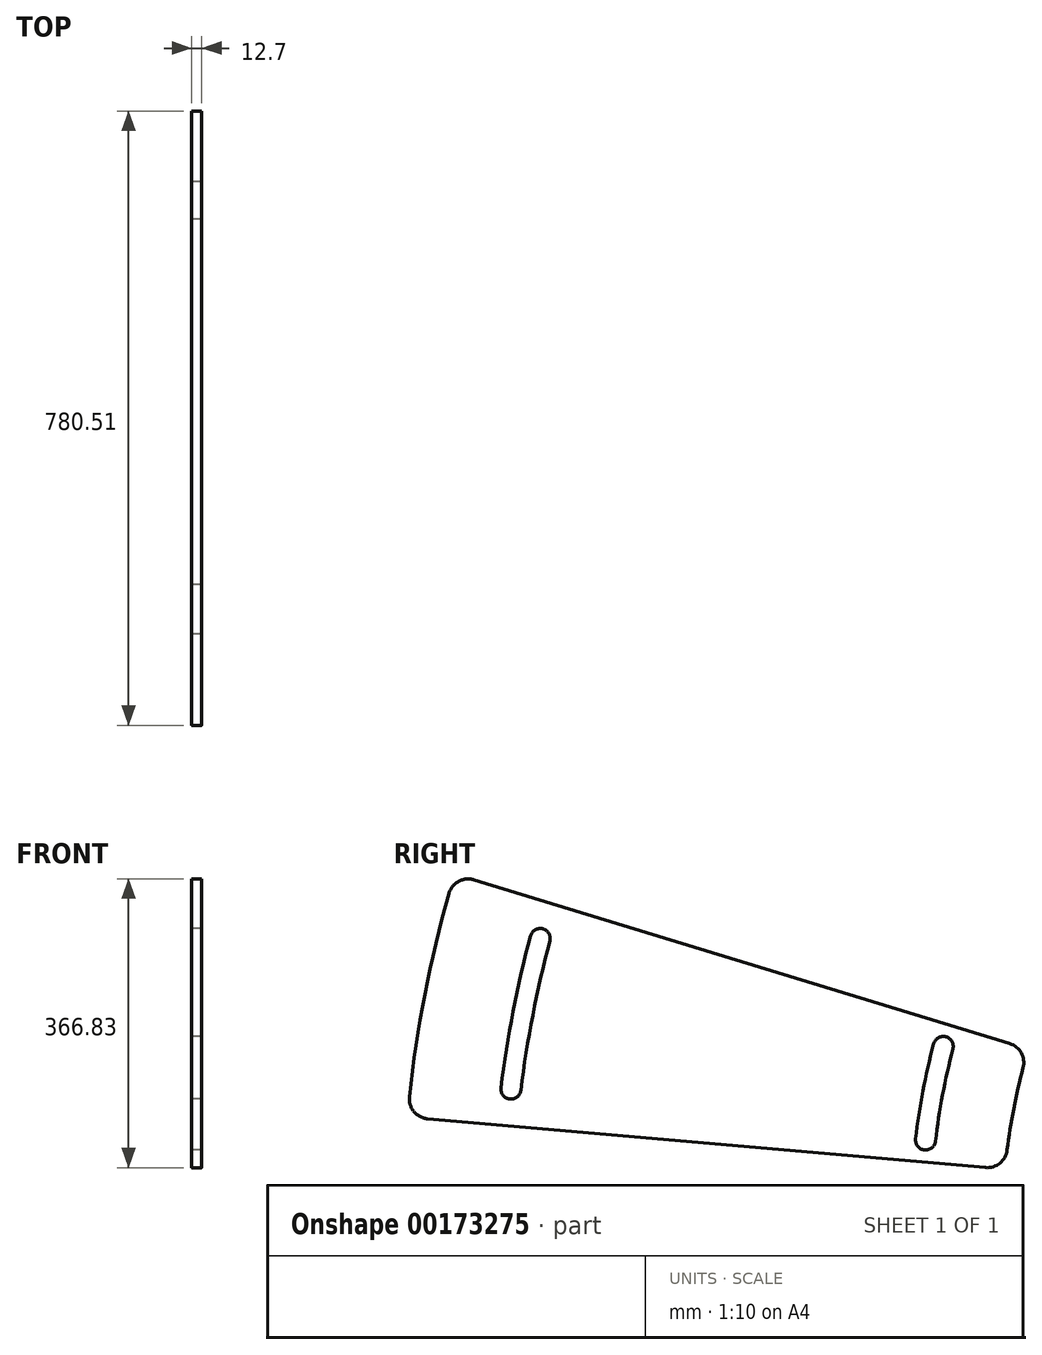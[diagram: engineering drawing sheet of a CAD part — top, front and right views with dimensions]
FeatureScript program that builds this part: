
annotation { "Feature Type Name" : "Feature", "Feature Type Description" : "" }
export const myFeature = defineFeature(function(context is Context, id is Id, definition is map)
    precondition{}
    {
        {
            var Q0;
            Q0=qCreatedBy(makeId("Right.planeOp"),FACE);
            var sketch = newSketch(context, id + "F0", { "sketchPlane" : qUnion([Q0])});
            skArc(sketch, "E0", {"start": v(-736.01, 197.3) * mm, "mid": v(-748, 145.4) * mm, "end": v(-756.33, 92.77) * mm});
            skLineSegment(sketch, "E1", {"start": v(0, 0) * mm, "end": v(-6.79, 0) * mm, "construction": true});
            skLineSegment(sketch, "E2", {"start": v(0, 0) * mm, "end": v(-1486.5, 288.95) * mm, "construction": true});
            skArc(sketch, "E3", {"start": v(-1465.3, 418.87) * mm, "mid": v(-1496, 290.8) * mm, "end": v(-1515.52, 160.55) * mm});
            skLineSegment(sketch, "E4", {"start": v(22.77, 0) * mm, "end": v(-18.63, 3.62) * mm});
            skArc(sketch, "E5", {"start": v(-837.45, 224.4) * mm, "mid": v(-850.72, 165.37) * mm, "end": v(-859.94, 105.59) * mm, "construction": true});
            skArc(sketch, "E6", {"start": v(-1349.4, 361.57) * mm, "mid": v(-1371.33, 266.56) * mm, "end": v(-1386.59, 170.25) * mm, "construction": true});
            skLineSegment(sketch, "E7.MirrorCS", {"start": v(21.1, -8.53) * mm, "end": v(-18.63, 3.62) * mm});
            skLineSegment(sketch, "E8.trimOffspring", {"start": v(-753.12, 228.18) * mm, "end": v(-1433.46, 436.18) * mm});
            skLineSegment(sketch, "E9.trimOffspring", {"start": v(-783.76, 70.56) * mm, "end": v(-1492.48, 132.57) * mm});
            skLineSegment(sketch, "E10.trimOffspring", {"start": v(-762, 0) * mm, "end": v(-1563.5, 0) * mm, "construction": true});
            skPoint(sketch, "E11.orphan", {"position": v(-1640.89, 499.6) * mm});
            skLineSegment(sketch, "E12", {"start": v(0, 0) * mm, "end": v(-1563.38, 191.96) * mm, "construction": true});
            skLineSegment(sketch, "E13", {"start": v(0, 0) * mm, "end": v(0, 0) * mm});
            skLineSegment(sketch, "E14.MirrorCS", {"start": v(0, 0) * mm, "end": v(-1521.45, 407.67) * mm, "construction": true});
            skArc(sketch, "E15.trimOffspring", {"start": v(-862.85, 77.48) * mm, "mid": v(-865.39, 38.78) * mm, "end": v(-866.23, 0) * mm, "construction": true});
            skArc(sketch, "E16.trimOffspring", {"start": v(-1391.5, 123.73) * mm, "mid": v(1371.33, -266.56) * mm, "end": v(-1336.54, 406.55) * mm, "construction": true});
            skArc(sketch, "E17.0.startCap", {"start": v(-1361.67, 364.86) * mm, "mid": v(-1346.11, 373.84) * mm, "end": v(-1337.13, 358.28) * mm});
            skArc(sketch, "E17.0.endCap", {"start": v(-1373.98, 168.7) * mm, "mid": v(-1388.13, 157.65) * mm, "end": v(-1399.2, 171.8) * mm});
            skArc(sketch, "E17.0.left", {"start": v(-1337.13, 358.28) * mm, "mid": v(-1358.87, 264.14) * mm, "end": v(-1373.98, 168.7) * mm});
            skArc(sketch, "E17.0.right", {"start": v(-1361.67, 364.86) * mm, "mid": v(-1383.8, 268.98) * mm, "end": v(-1399.2, 171.8) * mm});
            skArc(sketch, "E18.0.startCap", {"start": v(-849.74, 227.6) * mm, "mid": v(-834.24, 236.68) * mm, "end": v(-825.16, 221.19) * mm});
            skArc(sketch, "E18.0.endCap", {"start": v(-847.33, 104.08) * mm, "mid": v(-861.45, 92.98) * mm, "end": v(-872.55, 107.1) * mm});
            skArc(sketch, "E18.0.left", {"start": v(-825.16, 221.19) * mm, "mid": v(-838.24, 163.01) * mm, "end": v(-847.33, 104.08) * mm});
            skArc(sketch, "E18.0.right", {"start": v(-849.74, 227.6) * mm, "mid": v(-863.2, 167.74) * mm, "end": v(-872.55, 107.1) * mm});
            skPoint(sketch, "E19.visualSharp", {"position": v(-1457.99, 443.68) * mm});
            skArc(sketch, "E19.filletArc", {"start": v(-1433.46, 436.18) * mm, "mid": v(-1453.01, 434.2) * mm, "end": v(-1465.3, 418.87) * mm});
            skPoint(sketch, "E20.visualSharp", {"position": v(-729.28, 220.89) * mm});
            skArc(sketch, "E20.filletArc", {"start": v(-736.01, 197.3) * mm, "mid": v(-738.33, 216.2) * mm, "end": v(-753.12, 228.18) * mm});
            skPoint(sketch, "E21.visualSharp", {"position": v(-758.92, 68.39) * mm});
            skArc(sketch, "E21.filletArc", {"start": v(-783.76, 70.56) * mm, "mid": v(-765.56, 76.13) * mm, "end": v(-756.33, 92.77) * mm});
            skPoint(sketch, "E22.newPointA", {"position": v(-1708.56, 151.47) * mm});
            skArc(sketch, "E22.filletArc", {"start": v(-1515.52, 160.55) * mm, "mid": v(-1509.87, 141.72) * mm, "end": v(-1492.48, 132.57) * mm});
            skSolve(sketch);
        }
        {
            var Q0;
            Q0=makeQuery(id+"F0.imprint","IMPRINT",FACE,{"disambiguationData":[TD([[makeQuery(id+"F0.imprint","IMPRINT",EDGE,{"derivedFrom":sQuery(id+"F0.wireOp",EDGE,"E0")}),-1.0]])]});
            extrude(context, id + "F1", {"entities" : qUnion([Q0]), "depth" : 12.7 * mm});
        }
    });
